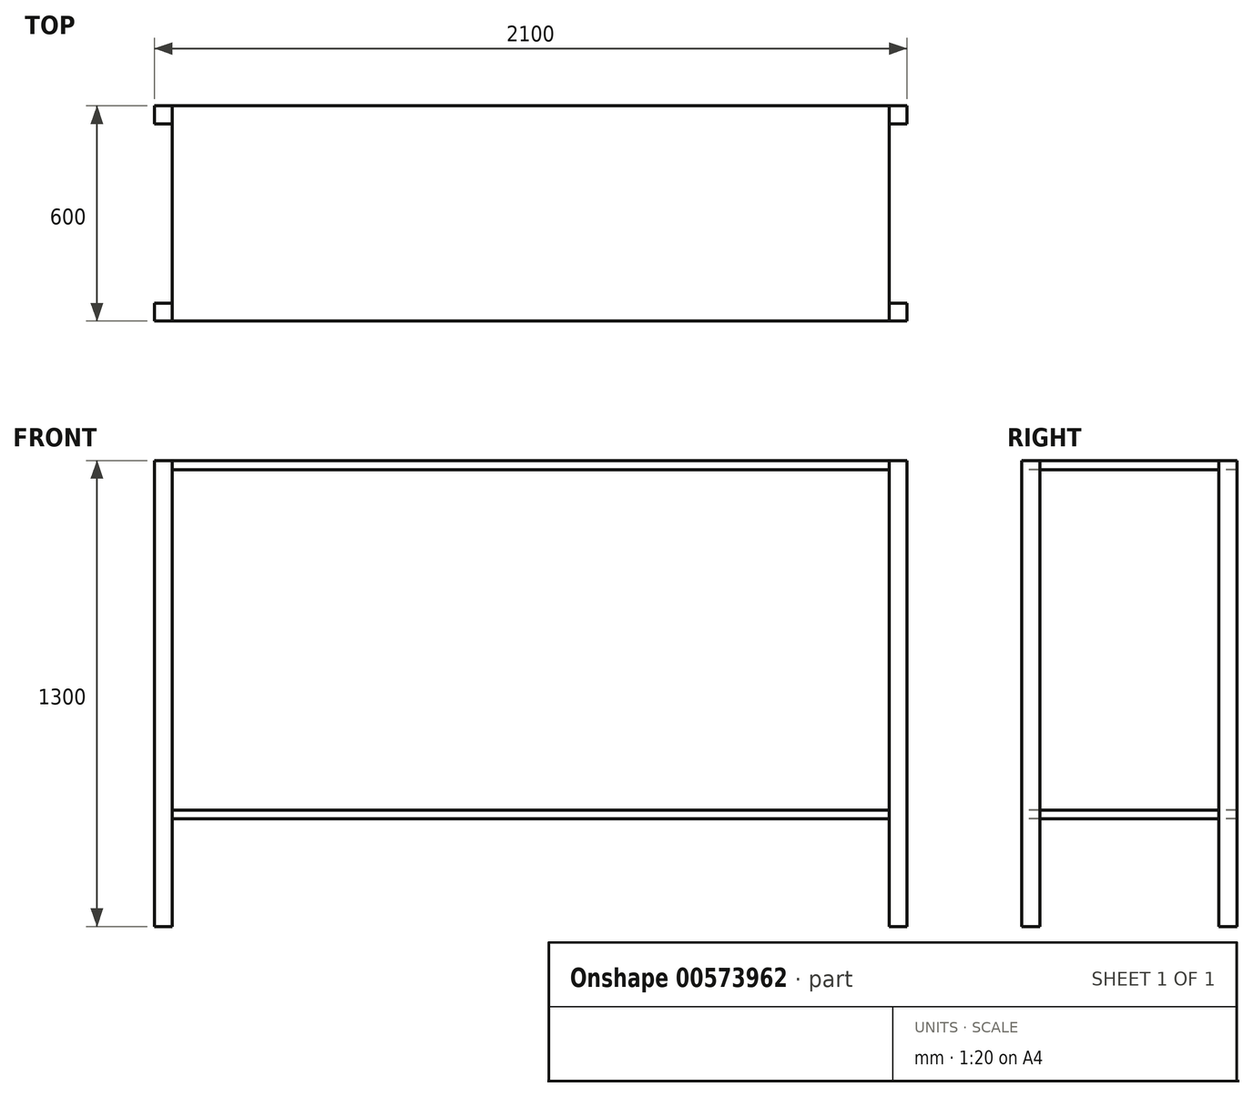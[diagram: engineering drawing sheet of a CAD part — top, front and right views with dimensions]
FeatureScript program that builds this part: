
annotation { "Feature Type Name" : "Feature", "Feature Type Description" : "" }
export const myFeature = defineFeature(function(context is Context, id is Id, definition is map)
    precondition{}
    {
        {
            var Q0;
            Q0=qCreatedBy(makeId("Top.planeOp"),FACE);
            cPlane(context, id + "F0", {"entities" : qUnion([Q0]), "cplaneType" : CPlaneType.OFFSET, "offset" : 300 * mm, "width" : 150 * mm, "height" : 150 * mm});
        }
        {
            var Q0;
            Q0=qCreatedBy(makeId("Top.planeOp"),FACE);
            cPlane(context, id + "F1", {"entities" : qUnion([Q0]), "cplaneType" : CPlaneType.OFFSET, "offset" : 1300 * mm, "width" : 150 * mm, "height" : 150 * mm});
        }
        {
            var Q0;
            Q0=qCreatedBy(makeId("Top.planeOp"),FACE);
            var sketch = newSketch(context, id + "F2", { "sketchPlane" : qUnion([Q0])});
            skPoint(sketch, "E0.middle", {"position": v(0, 0) * mm});
            skLineSegment(sketch, "E1.bottom", {"start": v(-1050, 300) * mm, "end": v(-1000, 300) * mm});
            skLineSegment(sketch, "E1.top", {"start": v(-1050, 250) * mm, "end": v(-1000, 250) * mm});
            skLineSegment(sketch, "E1.left", {"start": v(-1050, 300) * mm, "end": v(-1050, 250) * mm});
            skLineSegment(sketch, "E1.right", {"start": v(-1000, 300) * mm, "end": v(-1000, 250) * mm});
            skLineSegment(sketch, "E2.bottom", {"start": v(-1050, -300) * mm, "end": v(-1000, -300) * mm});
            skLineSegment(sketch, "E2.top", {"start": v(-1050, -250) * mm, "end": v(-1000, -250) * mm});
            skLineSegment(sketch, "E2.left", {"start": v(-1050, -300) * mm, "end": v(-1050, -250) * mm});
            skLineSegment(sketch, "E2.right", {"start": v(-1000, -300) * mm, "end": v(-1000, -250) * mm});
            skLineSegment(sketch, "E3.bottom", {"start": v(1050, -300) * mm, "end": v(1000, -300) * mm});
            skLineSegment(sketch, "E3.top", {"start": v(1050, -250) * mm, "end": v(1000, -250) * mm});
            skLineSegment(sketch, "E3.left", {"start": v(1050, -300) * mm, "end": v(1050, -250) * mm});
            skLineSegment(sketch, "E3.right", {"start": v(1000, -300) * mm, "end": v(1000, -250) * mm});
            skLineSegment(sketch, "E4.bottom", {"start": v(1050, 300) * mm, "end": v(1000, 300) * mm});
            skLineSegment(sketch, "E4.top", {"start": v(1050, 250) * mm, "end": v(1000, 250) * mm});
            skLineSegment(sketch, "E4.left", {"start": v(1050, 300) * mm, "end": v(1050, 250) * mm});
            skLineSegment(sketch, "E4.right", {"start": v(1000, 300) * mm, "end": v(1000, 250) * mm});
            skSolve(sketch);
        }
        {
            var Q0;
            Q0=qCreatedBy(id+"F0.planeOp",FACE);
            var sketch = newSketch(context, id + "F3", { "sketchPlane" : qUnion([Q0])});
            skLineSegment(sketch, "E5.bottom", {"start": v(1000, 300) * mm, "end": v(-1000, 300) * mm});
            skLineSegment(sketch, "E5.top", {"start": v(1000, -300) * mm, "end": v(-1000, -300) * mm});
            skLineSegment(sketch, "E5.left", {"start": v(1000, 300) * mm, "end": v(1000, -300) * mm});
            skLineSegment(sketch, "E5.right", {"start": v(-1000, 300) * mm, "end": v(-1000, -300) * mm});
            skPoint(sketch, "E5.middle", {"position": v(0, 0) * mm});
            skSolve(sketch);
        }
        {
            var Q0;
            Q0=qCreatedBy(id+"F1.planeOp",FACE);
            var sketch = newSketch(context, id + "F4", { "sketchPlane" : qUnion([Q0])});
            skLineSegment(sketch, "E6.bottom", {"start": v(1000, 300) * mm, "end": v(-1000, 300) * mm});
            skLineSegment(sketch, "E6.top", {"start": v(1000, -300) * mm, "end": v(-1000, -300) * mm});
            skLineSegment(sketch, "E6.left", {"start": v(1000, 300) * mm, "end": v(1000, -300) * mm});
            skLineSegment(sketch, "E6.right", {"start": v(-1000, 300) * mm, "end": v(-1000, -300) * mm});
            skPoint(sketch, "E6.middle", {"position": v(0, 0) * mm});
            skSolve(sketch);
        }
        {
            var Q0;
            Q0 = qSketchRegion(id + "F2", true);
            extrude(context, id + "F5", {"entities" : qUnion([Q0]), "depth" : 1300 * mm, "offsetDistance" : 25 * mm});
        }
        {
            var Q0;
            Q0 = qSketchRegion(id + "F3", true);
            extrude(context, id + "F6", {"entities" : qUnion([Q0]), "depth" : 25 * mm, "offsetDistance" : 25 * mm});
        }
        {
            var Q0;
            Q0 = qSketchRegion(id + "F4", true);
            extrude(context, id + "F7", {"entities" : qUnion([Q0]), "oppositeDirection" : true, "depth" : 25 * mm, "offsetDistance" : 25 * mm});
        }
    });
